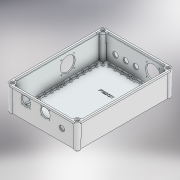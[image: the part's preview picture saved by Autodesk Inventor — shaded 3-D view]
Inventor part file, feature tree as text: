
AUTODESK INVENTOR PART (.ipt)
format: ipt  version: 2020 (Build 240168000, 168)  size: 667,648 bytes
history: native  units: mm
features: sketch x11, extrude x9, hole x4
ambient origin geometry x8: Origin, YZ Plane, XZ Plane, XY Plane, X Axis, Y Axis, Z Axis, Center Point
bodies: Solid1 (feature_tree)
feature tree (24):
  hole  "Hole1"  [1 undecoded]
  hole  "Hole2"  [1 undecoded]
  hole  "Hole3"  [1 undecoded]
  hole  "Hole4"  [1 undecoded]
  extrude  "Extrusion1"  Depth=2.0mm
  extrude  "Extrusion2"  Depth=32.0mm
  extrude  "Extrusion3"  Depth=32.0mm
  extrude  "Extrusion4"  Depth=2.0mm
  extrude  "Extrusion5"  TaperAngle=0.0deg  [1 undecoded]
  extrude  "Extrusion7"  TaperAngle=0.0deg  [1 undecoded]
  extrude  "Extrusion8"  Depth=10.0mm
  extrude  "Extrusion9"  TaperAngle=0.0deg  [1 undecoded]
  sketch  "Sketch1"  dims[d0=52.0mm d1=32.0mm]
  sketch  "Sketch3"  dims[d2=32.0mm d3=32.0mm]
  sketch  "Sketch4"  dims[d4=45.0mm d5=32.0mm]
  sketch  "Sketch5"  dims[d6=52.0mm d7=0.0mm]
  sketch  "Sketch6"  dims[d8=3.6mm d9=6.0mm d10=6.0mm d11=2.0mm d12=90.0deg d13=8.0mm d14=20.594885mm d15=52.0mm]
  sketch  "Sketch7"  dims[d16=52.0mm d17=32.0mm]
  sketch  "Sketch8"  dims[d18=32.0mm d21=32.0mm]
  sketch  "Sketch14"  dims[d22=32.0mm]
  sketch  "Sketch16"  dims[d23=3.6mm d24=6.0mm d25=6.0mm d26=2.0mm d27=90.0deg d28=8.0mm d29=20.594885mm d32=25.0mm]
  sketch  "Sketch17"  dims[d33=50.0mm d34=0.0mm]
  sketch  "Sketch20"  dims[d35=110.0mm d36=0.0mm d37=50.0mm d38=0.0mm d39=50.0mm d40=3.6mm d41=6.0mm d42=6.0mm d43=2.0mm d44=90.0deg d45=8.0mm d46=20.594885mm d47=35.0mm d48=0.0mm d49=50.0mm d50=0.0mm d51=50.0mm d52=0.0mm d53=50.0mm d54=25.0mm d55=3.6mm d56=6.0mm d57=6.0mm d58=2.0mm d59=90.0deg d60=8.0mm d61=20.594885mm d62=38.0mm d63=16.0mm d64=16.0mm d65=10.0mm d66=0.0mm d67=38.0mm d68=16.0mm d69=16.0mm d70=10.0mm d71=0.0mm d72=58.0mm d73=25.0mm d74=25.0mm d75=10.0mm d76=0.0mm d77=58.0mm d78=25.0mm d79=25.0mm d80=10.0mm d81=0.0mm d141=20.5mm d144=10.0mm d145=0.0mm d152=20.5mm d153=0.0mm d154=40.0mm d155=10.0mm d156=0.0mm d157=50.0mm d158=20.5mm d159=0.0mm d160=40.0mm d161=10.0mm d162=0.0mm d164=38.0mm d189=44.0mm d190=20.0mm d192=20.5mm d193=10.0mm d194=0.0mm d195=65.0mm]
  extrude  "Extrude4"  Depth=10.0mm
note: 7 required parameter values undecoded (feature->parameter linkage not recoverable at this tier; creation-order binding heuristic only, values carry confidence <= 0.55)
